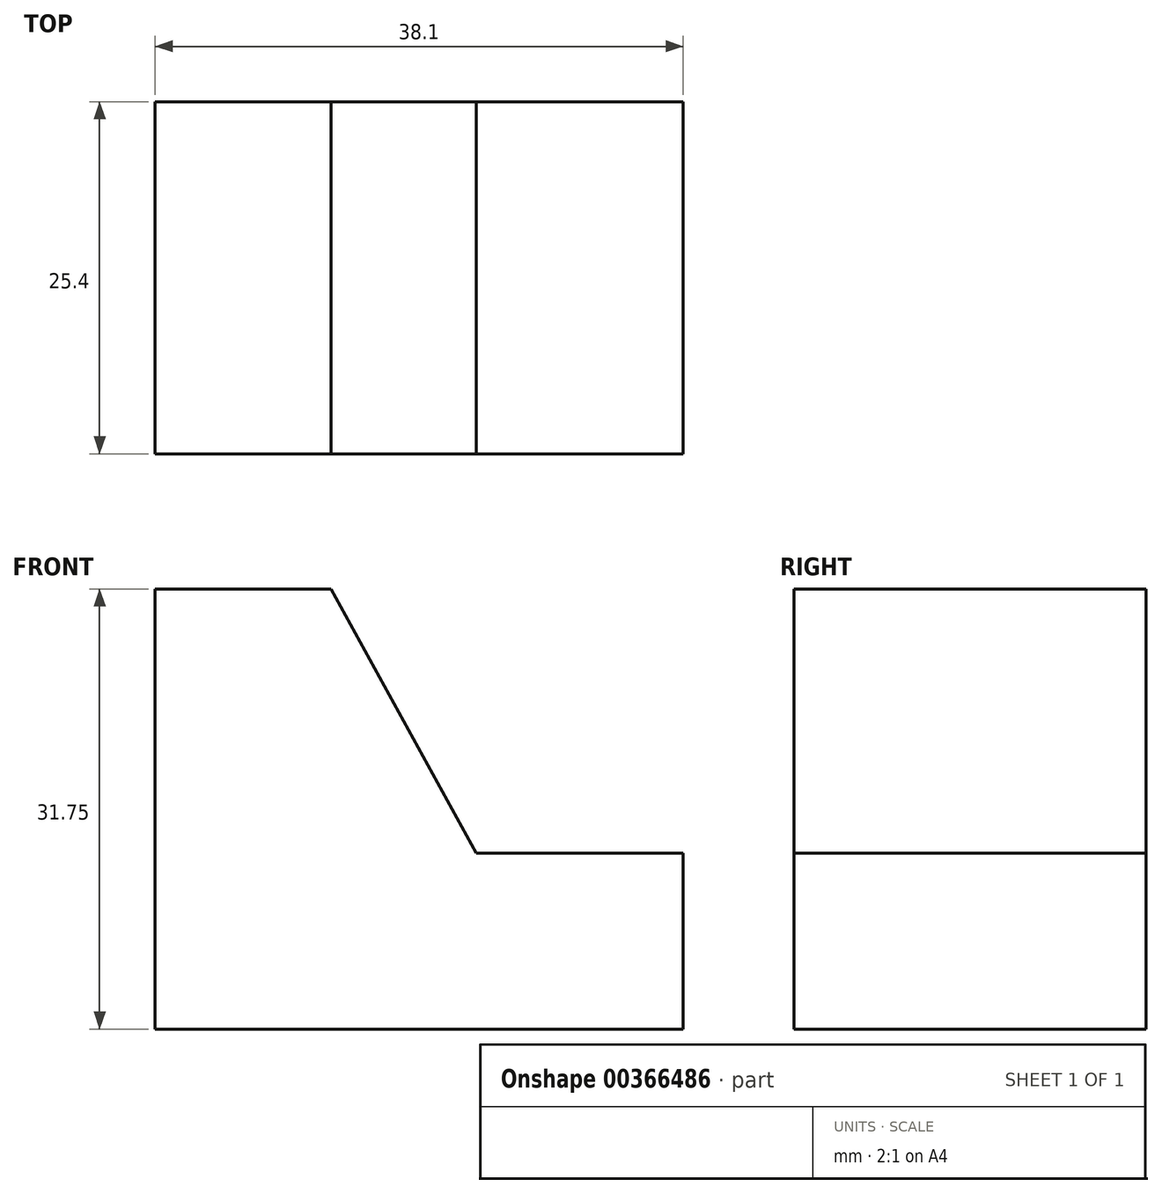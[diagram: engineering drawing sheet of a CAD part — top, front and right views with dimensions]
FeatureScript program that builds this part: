
annotation { "Feature Type Name" : "Feature", "Feature Type Description" : "" }
export const myFeature = defineFeature(function(context is Context, id is Id, definition is map)
    precondition{}
    {
        {
            var Q0;
            Q0=qCreatedBy(makeId("Front.planeOp"),FACE);
            var sketch = newSketch(context, id + "F0", { "sketchPlane" : qUnion([Q0])});
            skLineSegment(sketch, "E0", {"start": v(0, 0) * mm, "end": v(-23.16, 0) * mm});
            skLineSegment(sketch, "E1", {"start": v(-23.16, 0) * mm, "end": v(-23.16, 31.75) * mm});
            skLineSegment(sketch, "E2", {"start": v(-23.16, 31.75) * mm, "end": v(14.94, 31.75) * mm});
            skLineSegment(sketch, "E3", {"start": v(14.94, 31.75) * mm, "end": v(14.94, 0) * mm});
            skLineSegment(sketch, "E4", {"start": v(14.94, 0) * mm, "end": v(-23.16, 0) * mm});
            skSolve(sketch);
        }
        {
            var Q0;
            Q0 = qSketchRegion(id + "F0", true);
            extrude(context, id + "F1", {"entities" : qUnion([Q0]), "depth" : 25.4 * mm});
        }
        {
            var Q0;
            Q0=makeQuery(id+"F1.opExtrude","CAP_FACE",FACE,{"disambiguationData":[OSD([sQuery(id+"F0.wireOp",EDGE,"E1"),sQuery(id+"F0.wireOp",EDGE,"E2"),sQuery(id+"F0.wireOp",EDGE,"E3"),sQuery(id+"F0.wireOp",EDGE,"E4")])],"isStart":false});
            var sketch = newSketch(context, id + "F2", { "sketchPlane" : qUnion([Q0])});
            skLineSegment(sketch, "E5", {"start": v(-23.16, 31.75) * mm, "end": v(-10.46, 31.75) * mm});
            skLineSegment(sketch, "E6", {"start": v(-10.46, 31.75) * mm, "end": v(0, 12.7) * mm});
            skLineSegment(sketch, "E7", {"start": v(0, 12.7) * mm, "end": v(14.94, 12.7) * mm});
            skLineSegment(sketch, "E8", {"start": v(14.94, 12.7) * mm, "end": v(14.94, 31.75) * mm});
            skLineSegment(sketch, "E9", {"start": v(14.94, 31.75) * mm, "end": v(-10.46, 31.75) * mm});
            skSolve(sketch);
        }
        {
            var Q0;
            Q0 = qSketchRegion(id + "F2", true);
            extrude(context, id + "F3", {"entities" : qUnion([Q0]), "operationType" : NewBodyOperationType.REMOVE, "oppositeDirection" : true, "depth" : 25.4 * mm});
        }
    });
